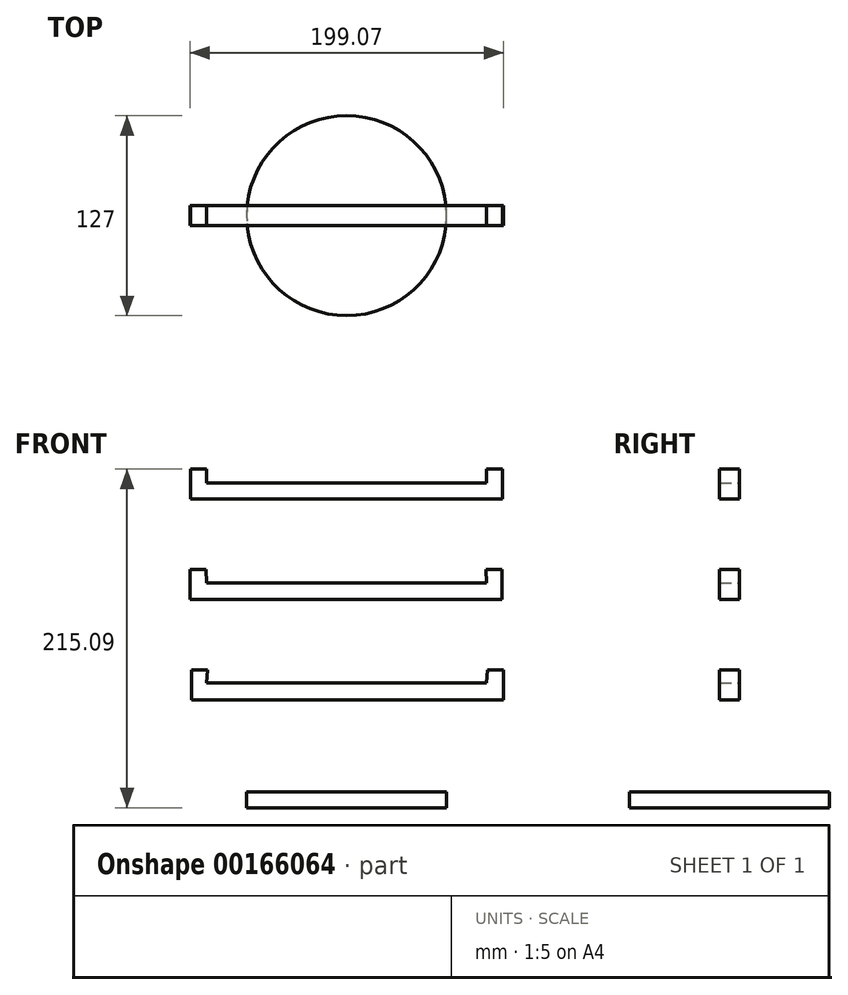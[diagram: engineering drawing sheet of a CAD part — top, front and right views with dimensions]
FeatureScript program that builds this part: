
annotation { "Feature Type Name" : "Feature", "Feature Type Description" : "" }
export const myFeature = defineFeature(function(context is Context, id is Id, definition is map)
    precondition{}
    {
        {
            var Q0;
            Q0=qCreatedBy(makeId("Top.planeOp"),FACE);
            var sketch = newSketch(context, id + "F0", { "sketchPlane" : qUnion([Q0])});
            skCircle(sketch, "E0", {"center": v(0, 0) * mm, "radius": 63.5 * mm});
            skSolve(sketch);
        }
        {
            var Q0;
            Q0=makeQuery(id+"F0.imprint","IMPRINT",FACE,{"disambiguationData":[TD([[makeQuery(id+"F0.imprint","IMPRINT",EDGE,{"derivedFrom":sQuery(id+"F0.wireOp",EDGE,"E0")}),1.0]])]});
            extrude(context, id + "F1", {"entities" : qUnion([Q0]), "depth" : 10.16 * mm});
        }
        {
            var Q0;
            Q0=makeQuery(id+"F1.opExtrude","CAP_FACE",FACE,{"disambiguationData":[OSD([sQuery(id+"F0.wireOp",EDGE,"E0")])],"isStart":false});
            var sketch = newSketch(context, id + "F2", { "sketchPlane" : qUnion([Q0])});
            skCircle(sketch, "E1", {"center": v(0, 0) * mm, "radius": 12.7 * mm});
            skSolve(sketch);
        }
        {
            var Q0;
            Q0=sQuery(id+"F2.wireOp",EDGE,"E1");
            extrude(context, id + "F3", {"bodyType" : ToolBodyType.SURFACE, "surfaceEntities" : qUnion([Q0]), "depth" : 248.92 * mm});
        }
        {
            var Q0;
            Q0=qCreatedBy(makeId("Front.planeOp"),FACE);
            var sketch = newSketch(context, id + "F4", { "sketchPlane" : qUnion([Q0])});
            skLineSegment(sketch, "E2", {"start": v(0, 0) * mm, "end": v(0, 10.62) * mm});
            skLineSegment(sketch, "E3", {"start": v(0, 10.62) * mm, "end": v(0, 74.12) * mm});
            skLineSegment(sketch, "E4", {"start": v(0, 74.12) * mm, "end": v(0, 137.62) * mm});
            skLineSegment(sketch, "E5", {"start": v(0, 137.62) * mm, "end": v(0, 201.12) * mm});
            skLineSegment(sketch, "E6.0", {"start": v(0, 79.2) * mm, "end": v(-88.9, 79.2) * mm});
            skLineSegment(sketch, "E6.1", {"start": v(0, 79.2) * mm, "end": v(88.9, 79.2) * mm});
            skLineSegment(sketch, "E7.0", {"start": v(0.57, 68.65) * mm, "end": v(89.47, 68.65) * mm});
            skLineSegment(sketch, "E7.1", {"start": v(0.57, 68.65) * mm, "end": v(-88.33, 68.65) * mm});
            skLineSegment(sketch, "E8", {"start": v(89.47, 87.7) * mm, "end": v(99.63, 87.7) * mm});
            skLineSegment(sketch, "E9", {"start": v(99.63, 87.7) * mm, "end": v(99.63, 68.65) * mm});
            skLineSegment(sketch, "E10", {"start": v(99.63, 68.65) * mm, "end": v(89.47, 68.65) * mm});
            skLineSegment(sketch, "E11", {"start": v(-88.33, 87.7) * mm, "end": v(-98.49, 87.7) * mm});
            skLineSegment(sketch, "E12", {"start": v(-98.49, 87.7) * mm, "end": v(-98.49, 68.65) * mm});
            skLineSegment(sketch, "E13", {"start": v(-88.33, 68.65) * mm, "end": v(-98.49, 68.65) * mm});
            skLineSegment(sketch, "E14.0", {"start": v(0, 142.7) * mm, "end": v(-88.9, 142.7) * mm});
            skLineSegment(sketch, "E14.1", {"start": v(0, 142.7) * mm, "end": v(88.9, 142.7) * mm});
            skLineSegment(sketch, "E15.0", {"start": v(-0.38, 132.37) * mm, "end": v(88.52, 132.37) * mm});
            skLineSegment(sketch, "E15.1", {"start": v(-0.38, 132.37) * mm, "end": v(-89.28, 132.37) * mm});
            skLineSegment(sketch, "E16", {"start": v(-89.28, 151.42) * mm, "end": v(-99.44, 151.42) * mm});
            skLineSegment(sketch, "E17", {"start": v(-99.44, 151.42) * mm, "end": v(-99.44, 132.37) * mm});
            skLineSegment(sketch, "E18", {"start": v(-89.28, 132.37) * mm, "end": v(-99.44, 132.37) * mm});
            skLineSegment(sketch, "E19", {"start": v(88.52, 151.42) * mm, "end": v(98.68, 151.42) * mm});
            skLineSegment(sketch, "E20", {"start": v(98.68, 151.42) * mm, "end": v(98.68, 132.37) * mm});
            skLineSegment(sketch, "E21", {"start": v(98.68, 132.37) * mm, "end": v(88.52, 132.37) * mm});
            skLineSegment(sketch, "E22.0", {"start": v(0, 206.2) * mm, "end": v(88.9, 206.2) * mm});
            skLineSegment(sketch, "E22.1", {"start": v(0, 206.2) * mm, "end": v(-88.9, 206.2) * mm});
            skLineSegment(sketch, "E23.0", {"start": v(0, 196.04) * mm, "end": v(88.9, 196.04) * mm});
            skLineSegment(sketch, "E23.1", {"start": v(0, 196.04) * mm, "end": v(-88.9, 196.04) * mm});
            skLineSegment(sketch, "E24", {"start": v(-88.9, 206.2) * mm, "end": v(-88.9, 215.1) * mm});
            skLineSegment(sketch, "E25", {"start": v(-88.9, 215.1) * mm, "end": v(-99.06, 215.1) * mm});
            skLineSegment(sketch, "E26", {"start": v(-99.06, 215.1) * mm, "end": v(-99.06, 196.04) * mm});
            skLineSegment(sketch, "E27", {"start": v(-99.06, 196.04) * mm, "end": v(-88.9, 196.04) * mm});
            skLineSegment(sketch, "E28", {"start": v(88.9, 215.1) * mm, "end": v(99.06, 215.1) * mm});
            skLineSegment(sketch, "E29", {"start": v(99.06, 215.1) * mm, "end": v(99.06, 196.04) * mm});
            skLineSegment(sketch, "E30", {"start": v(99.06, 196.04) * mm, "end": v(88.9, 196.04) * mm});
            skLineSegment(sketch, "E31", {"start": v(88.9, 142.7) * mm, "end": v(88.52, 151.42) * mm});
            skLineSegment(sketch, "E32", {"start": v(88.9, 206.2) * mm, "end": v(88.9, 215.1) * mm});
            skLineSegment(sketch, "E33", {"start": v(88.9, 79.2) * mm, "end": v(89.47, 87.7) * mm});
            skLineSegment(sketch, "E34", {"start": v(-88.9, 79.2) * mm, "end": v(-88.33, 87.7) * mm});
            skLineSegment(sketch, "E35", {"start": v(-88.9, 142.7) * mm, "end": v(-89.28, 151.42) * mm});
            skSolve(sketch);
        }
        {
            var Q0;
            Q0 = qSketchRegion(id + "F4", true);
            extrude(context, id + "F5", {"entities" : qUnion([Q0]), "endBound" : BoundingType.SYMMETRIC, "depth" : 12.7 * mm});
        }
    });
